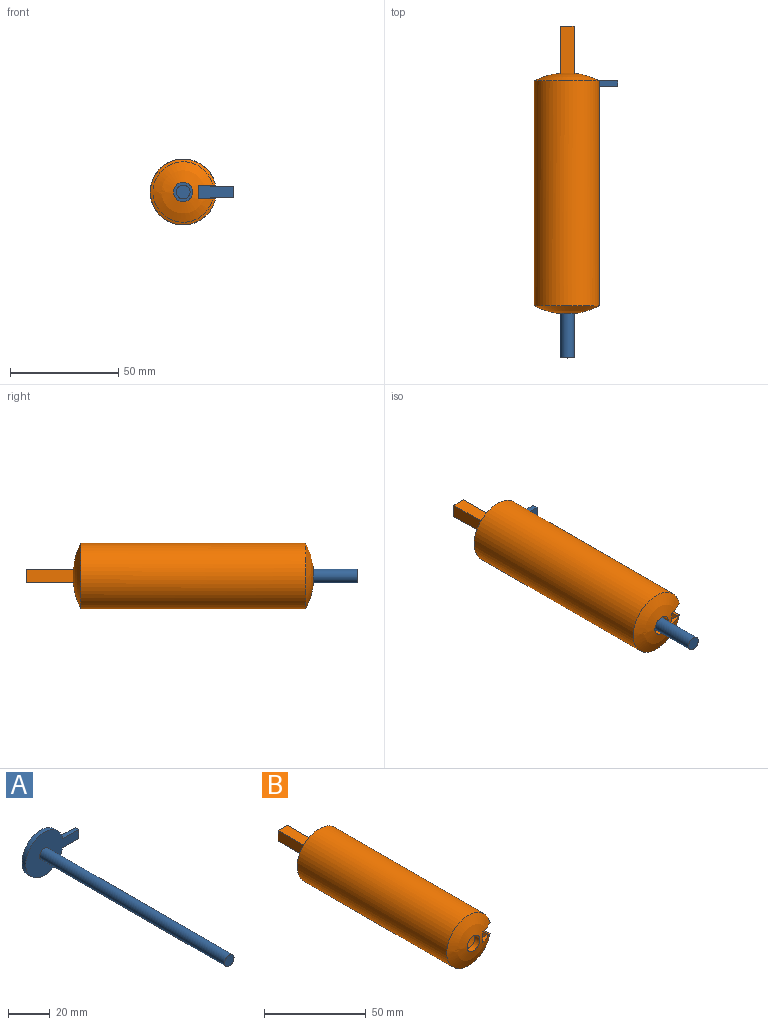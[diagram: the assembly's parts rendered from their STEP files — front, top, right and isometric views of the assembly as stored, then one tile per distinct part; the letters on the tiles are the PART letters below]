
ASSEMBLY  parts=2 mates=1
PART A: 8 faces, bbox 36.1x128.3x25.4 mm
  f0: cylinder r=12.7mm len=25.4mm, axis (0,1,0), area 189.2mm2, adj f1,f2,f5,f7
  f1: plane 36.07x25.4mm, normal (0,-1,0), area 531.6mm2, adj f0,f3,f5,f6,f7
  f2: plane 36.07x25.4mm, normal (0,1,0), area 563.3mm2, adj f0,f5,f6,f7
  f3: cylinder r=3.17mm len=125.73mm, axis (0,1,0), area 2508.2mm2, adj f1,f4
  f4: plane 6.35x6.35mm, normal (0,-1,0), area 31.7mm2, adj f3
  f5: plane 10.93x2.54mm, normal (0,0,1), area 27.7mm2, adj f0,f1,f2,f6
  f6: plane 5.25x2.54mm, normal (1,0,0), area 13.3mm2, adj f1,f2,f5,f7
  f7: plane 10.97x2.54mm, normal (0,0,-1), area 27.9mm2, adj f0,f1,f2,f6
PART B: 16 faces, bbox 30.5x133x30.5 mm
  f0: sphere r=33.12mm, area 676.6mm2, adj f2,f7,f8,f9,f11,f12,f13,f14
  f1: sphere r=33.12mm, area 654.7mm2, adj f2,f6,f8,f9,f10
  f2: cylinder r=15.24mm len=104.14mm, axis (0,1,0), area 9305.8mm2, adj f0,f1,f8,f9
  f3: cylinder r=13.97mm len=104.14mm, axis (0,1,0), area 8473.9mm2, adj f4,f5,f8,f9
  f4: plane 27.94x27.57mm, normal (0,-1,0), area 568.7mm2, adj f3,f7,f8,f9
  f5: plane 27.94x27.57mm, normal (0,1,0), area 506.7mm2, adj f3,f6,f8,f9,f10
  f6: cylinder r=4.45mm len=8.89mm, axis (0,1,0), area 95.4mm2, adj f1,f5
  f7: plane 6.35x3mm, normal (1,0,0), area 18.7mm2, adj f0,f4,f8,f9
  f8: plane 109.82x8.05mm, normal (0,0,-1), area 161.5mm2, adj f0,f1,f2,f3,f4,f5,f7,f10
  f9: plane 109.82x8.05mm, normal (0,0,1), area 161.5mm2, adj f0,f1,f2,f3,f4,f5,f7,f10
  f10: plane 6.35x3mm, normal (1,0,0), area 18.7mm2, adj f1,f5,f8,f9
  f11: plane 21.99x6.35mm, normal (-1,0,0), area 139mm2, adj f0,f12,f14,f15
  f12: plane 21.99x6.35mm, normal (0,0,-1), area 139mm2, adj f0,f11,f13,f15
  f13: plane 21.99x6.35mm, normal (1,0,0), area 139mm2, adj f0,f12,f14,f15
  f14: plane 21.99x6.35mm, normal (0,0,1), area 139mm2, adj f0,f11,f13,f15
  f15: plane 6.35x6.35mm, normal (0,1,0), area 40.3mm2, adj f11,f12,f13,f14
PLACE A t=(0,50.8,0)mm
PLACE B at identity fixed
MATE slider A.f0 <-> B.f3  axis (0,1,0) through (0,52.07,0)mm
